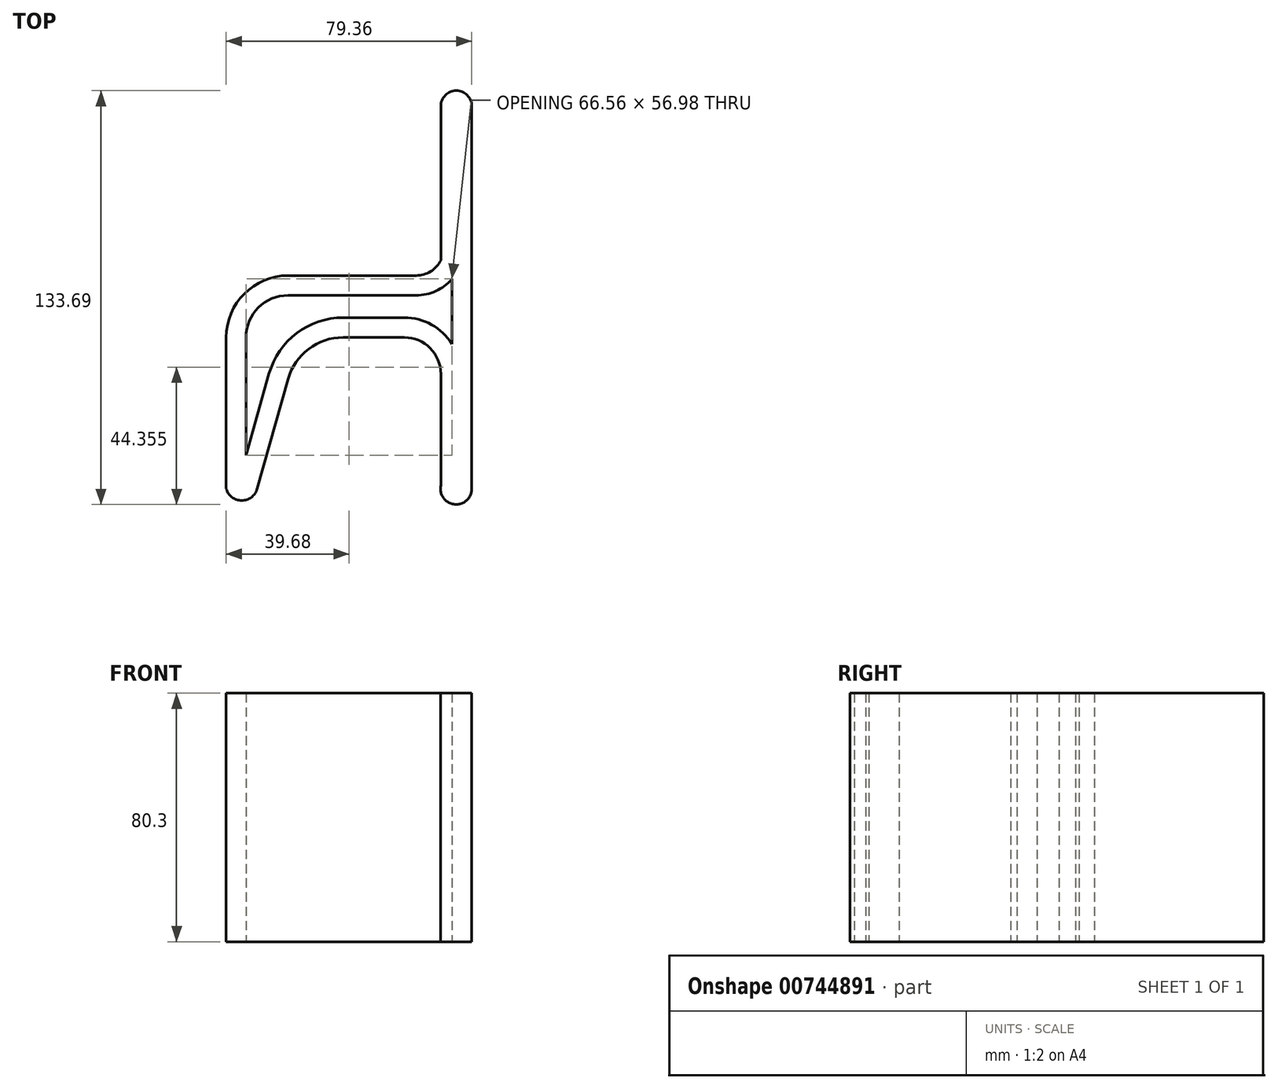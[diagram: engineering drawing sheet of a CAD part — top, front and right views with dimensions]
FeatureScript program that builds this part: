
annotation { "Feature Type Name" : "Feature", "Feature Type Description" : "" }
export const myFeature = defineFeature(function(context is Context, id is Id, definition is map)
    precondition{}
    {
        {
            var Q0;
            Q0=qCreatedBy(makeId("Top.planeOp"),FACE);
            var sketch = newSketch(context, id + "F0", { "sketchPlane" : qUnion([Q0])});
            skLineSegment(sketch, "E0", {"start": v(-36.77, -56.58) * mm, "end": v(-36.77, -7.67) * mm});
            skArc(sketch, "E1", {"start": v(-36.77, -7.67) * mm, "mid": v(-30.91, 6.48) * mm, "end": v(-16.77, 12.33) * mm});
            skLineSegment(sketch, "E2", {"start": v(-16.77, 12.33) * mm, "end": v(24.6, 12.33) * mm});
            skArc(sketch, "E3", {"start": v(24.6, 12.33) * mm, "mid": v(29.29, 13.66) * mm, "end": v(32.59, 17.24) * mm});
            skLineSegment(sketch, "E4", {"start": v(32.59, 17.24) * mm, "end": v(32.59, 67.06) * mm});
            skArc(sketch, "E5", {"start": v(32.59, 67.06) * mm, "mid": v(37.59, 72.06) * mm, "end": v(42.59, 67.06) * mm});
            skLineSegment(sketch, "E6", {"start": v(42.59, 67.06) * mm, "end": v(42.59, -56.58) * mm});
            skArc(sketch, "E7", {"start": v(42.59, -56.58) * mm, "mid": v(37.03, -61.6) * mm, "end": v(32.59, -55.57) * mm});
            skLineSegment(sketch, "E8", {"start": v(32.59, -55.57) * mm, "end": v(32.59, -19.5) * mm});
            skArc(sketch, "E9", {"start": v(32.59, -19.5) * mm, "mid": v(29.13, -11.13) * mm, "end": v(20.77, -7.67) * mm});
            skLineSegment(sketch, "E10", {"start": v(20.77, -7.67) * mm, "end": v(1, -7.67) * mm});
            skArc(sketch, "E11", {"start": v(1, -7.67) * mm, "mid": v(-10.14, -11.41) * mm, "end": v(-16.77, -21.12) * mm});
            skLineSegment(sketch, "E12", {"start": v(-16.77, -21.12) * mm, "end": v(-26.77, -56.58) * mm});
            skArc(sketch, "E13", {"start": v(-26.77, -56.58) * mm, "mid": v(-31.77, -60.36) * mm, "end": v(-36.77, -56.58) * mm});
            skArc(sketch, "E14.0", {"start": v(24.6, 5.93) * mm, "mid": v(30.97, 7.32) * mm, "end": v(36.19, 11.21) * mm});
            skLineSegment(sketch, "E14.1", {"start": v(-16.77, 5.93) * mm, "end": v(24.6, 5.93) * mm});
            skLineSegment(sketch, "E14.2", {"start": v(36.19, 11.21) * mm, "end": v(36.19, -9.78) * mm});
            skArc(sketch, "E14.3", {"start": v(-30.37, -7.67) * mm, "mid": v(-26.39, 1.95) * mm, "end": v(-16.77, 5.93) * mm});
            skLineSegment(sketch, "E14.4", {"start": v(-30.37, -45.77) * mm, "end": v(-30.37, -7.67) * mm});
            skArc(sketch, "E14.5", {"start": v(36.19, -9.78) * mm, "mid": v(29.58, -3.54) * mm, "end": v(20.77, -1.27) * mm});
            skLineSegment(sketch, "E14.6", {"start": v(20.77, -1.27) * mm, "end": v(1, -1.27) * mm});
            skArc(sketch, "E14.7", {"start": v(1, -1.27) * mm, "mid": v(-14, -6.3) * mm, "end": v(-22.93, -19.38) * mm});
            skLineSegment(sketch, "E14.8", {"start": v(-22.93, -19.38) * mm, "end": v(-30.37, -45.77) * mm});
            skSolve(sketch);
        }
        {
            var Q0;
            Q0=makeQuery(id+"F0.imprint","IMPRINT",FACE,{"disambiguationData":[TD([[makeQuery(id+"F0.imprint","IMPRINT",EDGE,{"derivedFrom":sQuery(id+"F0.wireOp",EDGE,"E0")}),-1.0]])]});
            extrude(context, id + "F1", {"entities" : qUnion([Q0]), "depth" : 80.3 * mm, "offsetDistance" : 25 * mm});
        }
    });
